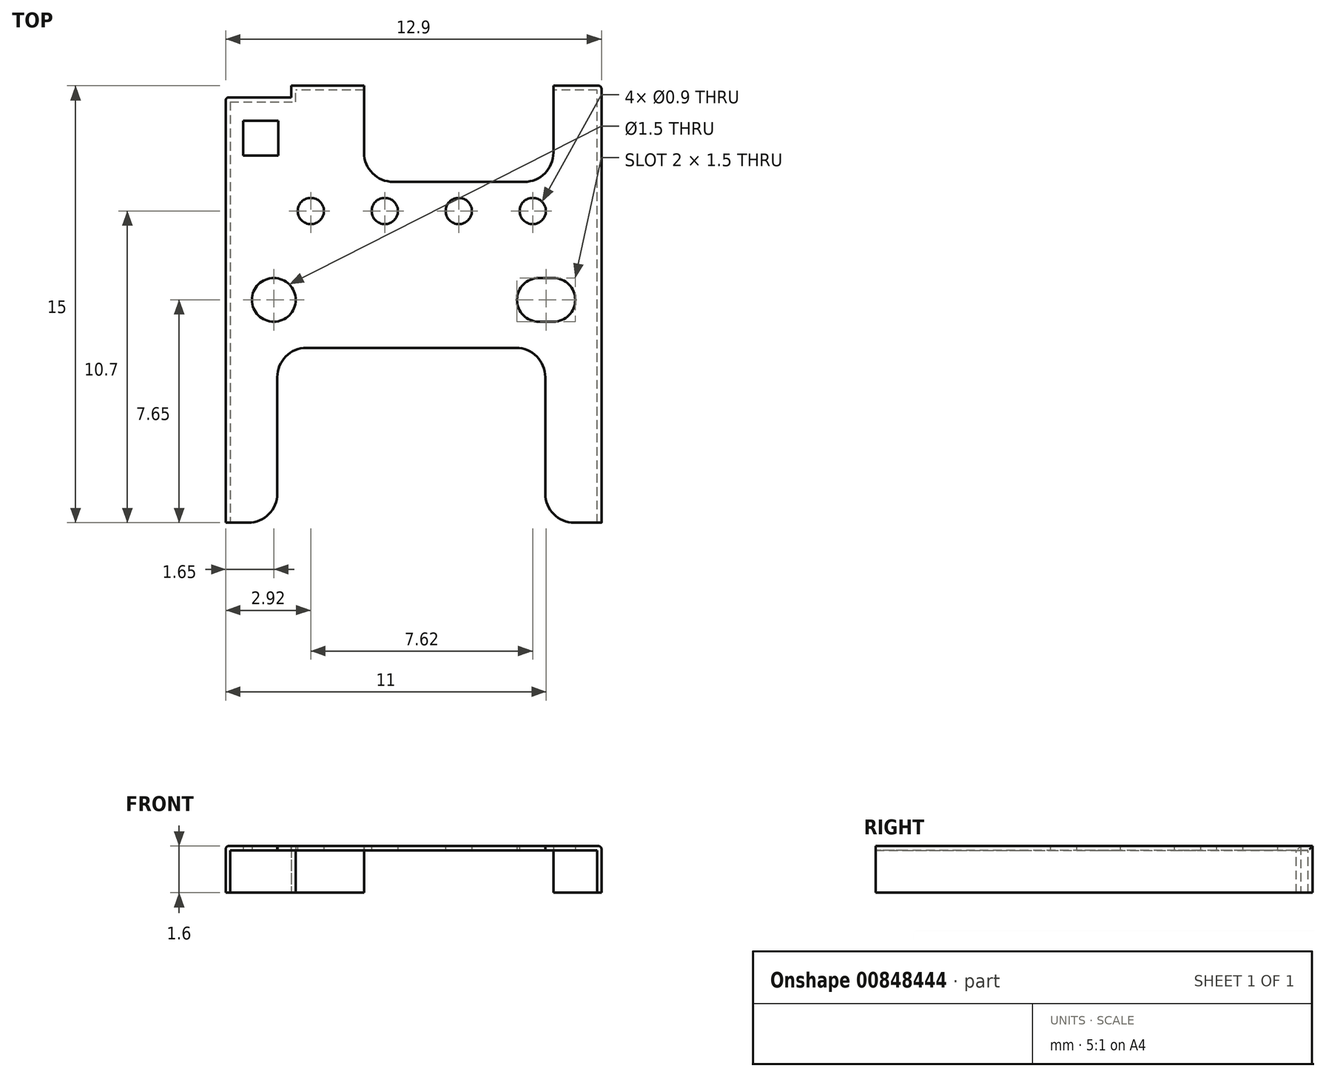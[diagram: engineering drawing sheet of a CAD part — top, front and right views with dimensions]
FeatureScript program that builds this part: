
annotation { "Feature Type Name" : "Feature", "Feature Type Description" : "" }
export const myFeature = defineFeature(function(context is Context, id is Id, definition is map)
    precondition{}
    {
        {
            var Q0;
            Q0=qCreatedBy(makeId("Top.planeOp"),FACE);
            var sketch = newSketch(context, id + "F0", { "sketchPlane" : qUnion([Q0])});
            skLineSegment(sketch, "E0.bottom", {"start": v(0, 0) * mm, "end": v(1.77, 0) * mm});
            skLineSegment(sketch, "E0.top", {"start": v(2.25, 15) * mm, "end": v(4.75, 15) * mm});
            skLineSegment(sketch, "E0.left", {"start": v(0, 0) * mm, "end": v(0, 14.6) * mm});
            skLineSegment(sketch, "E0.right", {"start": v(12.9, 0) * mm, "end": v(12.9, 15) * mm});
            skLineSegment(sketch, "E1.top", {"start": v(4.75, 11.7) * mm, "end": v(11.25, 11.7) * mm});
            skLineSegment(sketch, "E1.left", {"start": v(4.75, 15) * mm, "end": v(4.75, 11.7) * mm});
            skLineSegment(sketch, "E1.right", {"start": v(11.25, 15) * mm, "end": v(11.25, 11.7) * mm});
            skLineSegment(sketch, "E2.trimOffspring", {"start": v(11.25, 15) * mm, "end": v(12.9, 15) * mm});
            skLineSegment(sketch, "E3.bottom", {"start": v(0.6, 13.8) * mm, "end": v(1.8, 13.8) * mm});
            skLineSegment(sketch, "E3.top", {"start": v(0.6, 12.6) * mm, "end": v(1.8, 12.6) * mm});
            skLineSegment(sketch, "E3.left", {"start": v(0.6, 13.8) * mm, "end": v(0.6, 12.6) * mm});
            skLineSegment(sketch, "E3.right", {"start": v(1.8, 13.8) * mm, "end": v(1.8, 12.6) * mm});
            skLineSegment(sketch, "E4.top", {"start": v(0, 14.6) * mm, "end": v(2.25, 14.6) * mm});
            skLineSegment(sketch, "E4.right", {"start": v(2.25, 15) * mm, "end": v(2.25, 14.6) * mm});
            skCircle(sketch, "E5", {"center": v(5.46, 10.7) * mm, "radius": 0.45 * mm});
            skCircle(sketch, "E6", {"center": v(8, 10.7) * mm, "radius": 0.45 * mm});
            skCircle(sketch, "E7", {"center": v(10.54, 10.7) * mm, "radius": 0.45 * mm});
            skLineSegment(sketch, "E8", {"start": v(8, 11.7) * mm, "end": v(8, 10.7) * mm, "construction": true});
            skLineSegment(sketch, "E9", {"start": v(8, 10.7) * mm, "end": v(10.54, 10.7) * mm, "construction": true});
            skLineSegment(sketch, "E10", {"start": v(8, 10.7) * mm, "end": v(5.46, 10.7) * mm, "construction": true});
            skArc(sketch, "E11", {"start": v(11.25, 6.9) * mm, "mid": v(12, 7.65) * mm, "end": v(11.25, 8.4) * mm});
            skLineSegment(sketch, "E12", {"start": v(11.25, 7.65) * mm, "end": v(10.75, 7.65) * mm, "construction": true});
            skArc(sketch, "E13", {"start": v(10.75, 8.4) * mm, "mid": v(10, 7.65) * mm, "end": v(10.75, 6.9) * mm});
            skLineSegment(sketch, "E14", {"start": v(10.75, 8.4) * mm, "end": v(11.25, 8.4) * mm});
            skLineSegment(sketch, "E15", {"start": v(10.75, 6.9) * mm, "end": v(11.25, 6.9) * mm});
            skLineSegment(sketch, "E16", {"start": v(10.75, 7.65) * mm, "end": v(1.65, 7.65) * mm, "construction": true});
            skCircle(sketch, "E17", {"center": v(1.65, 7.65) * mm, "radius": 0.75 * mm});
            skLineSegment(sketch, "E18.top", {"start": v(1.77, 6) * mm, "end": v(10.97, 6) * mm});
            skLineSegment(sketch, "E18.left", {"start": v(1.77, 0) * mm, "end": v(1.77, 6) * mm});
            skLineSegment(sketch, "E18.right", {"start": v(10.97, 0) * mm, "end": v(10.97, 6) * mm});
            skCircle(sketch, "E19", {"center": v(2.92, 10.7) * mm, "radius": 0.45 * mm});
            skLineSegment(sketch, "E20", {"start": v(5.46, 10.7) * mm, "end": v(2.92, 10.7) * mm, "construction": true});
            skLineSegment(sketch, "E21.trimOffspring", {"start": v(10.97, 0) * mm, "end": v(12.9, 0) * mm});
            skSolve(sketch);
        }
        {
            var Q0;
            Q0=makeQuery(id+"F0.imprint","IMPRINT",FACE,{"disambiguationData":[TD([[makeQuery(id+"F0.imprint","IMPRINT",EDGE,{"derivedFrom":sQuery(id+"F0.wireOp",EDGE,"E0.bottom")}),1.0]])]});
            extrude(context, id + "F1", {"entities" : qUnion([Q0]), "depth" : 0.15 * mm, "offsetDistance" : 25 * mm});
        }
        {
            var Q0;
            Q0=makeQuery(id+"F1.opExtrude","CAP_FACE",FACE,{"disambiguationData":[OSD([sQuery(id+"F0.wireOp",EDGE,"E0.bottom"),sQuery(id+"F0.wireOp",EDGE,"E0.top"),sQuery(id+"F0.wireOp",EDGE,"E0.left"),sQuery(id+"F0.wireOp",EDGE,"E0.right"),sQuery(id+"F0.wireOp",EDGE,"E1.top"),sQuery(id+"F0.wireOp",EDGE,"E1.left"),sQuery(id+"F0.wireOp",EDGE,"E1.right"),sQuery(id+"F0.wireOp",EDGE,"E2.trimOffspring"),sQuery(id+"F0.wireOp",EDGE,"E3.bottom"),sQuery(id+"F0.wireOp",EDGE,"E3.top"),sQuery(id+"F0.wireOp",EDGE,"E3.left"),sQuery(id+"F0.wireOp",EDGE,"E3.right"),sQuery(id+"F0.wireOp",EDGE,"E4.top"),sQuery(id+"F0.wireOp",EDGE,"E4.right"),sQuery(id+"F0.wireOp",EDGE,"E5"),sQuery(id+"F0.wireOp",EDGE,"E6"),sQuery(id+"F0.wireOp",EDGE,"E7"),sQuery(id+"F0.wireOp",EDGE,"E11"),sQuery(id+"F0.wireOp",EDGE,"E13"),sQuery(id+"F0.wireOp",EDGE,"E14"),sQuery(id+"F0.wireOp",EDGE,"E15"),sQuery(id+"F0.wireOp",EDGE,"E17"),sQuery(id+"F0.wireOp",EDGE,"E18.top"),sQuery(id+"F0.wireOp",EDGE,"E18.left"),sQuery(id+"F0.wireOp",EDGE,"E18.right"),sQuery(id+"F0.wireOp",EDGE,"E19"),sQuery(id+"F0.wireOp",EDGE,"E21.trimOffspring")])],"isStart":true});
            var sketch = newSketch(context, id + "F2", { "sketchPlane" : qUnion([Q0])});
            skLineSegment(sketch, "E22.bottom", {"start": v(12.9, 0) * mm, "end": v(12.75, 0) * mm});
            skLineSegment(sketch, "E22.top", {"start": v(12.9, -15) * mm, "end": v(12.75, -15) * mm});
            skLineSegment(sketch, "E22.left", {"start": v(12.9, 0) * mm, "end": v(12.9, -15) * mm});
            skLineSegment(sketch, "E22.right", {"start": v(12.75, 0) * mm, "end": v(12.75, -15) * mm});
            skLineSegment(sketch, "E23.bottom", {"start": v(12.75, -14.85) * mm, "end": v(11.25, -14.85) * mm});
            skLineSegment(sketch, "E23.top", {"start": v(12.75, -15) * mm, "end": v(11.25, -15) * mm});
            skLineSegment(sketch, "E23.left", {"start": v(12.75, -14.85) * mm, "end": v(12.75, -15) * mm});
            skLineSegment(sketch, "E23.right", {"start": v(11.25, -14.85) * mm, "end": v(11.25, -15) * mm});
            skLineSegment(sketch, "E24.bottom", {"start": v(4.75, -14.85) * mm, "end": v(2.25, -14.85) * mm});
            skLineSegment(sketch, "E24.top", {"start": v(4.75, -15) * mm, "end": v(2.25, -15) * mm});
            skLineSegment(sketch, "E24.left", {"start": v(4.75, -14.85) * mm, "end": v(4.75, -15) * mm});
            skLineSegment(sketch, "E24.right", {"start": v(2.25, -14.85) * mm, "end": v(2.25, -15) * mm});
            skLineSegment(sketch, "E25.bottom", {"start": v(0, -14.6) * mm, "end": v(2.25, -14.6) * mm});
            skLineSegment(sketch, "E25.top", {"start": v(0, -14.45) * mm, "end": v(2.25, -14.45) * mm});
            skLineSegment(sketch, "E25.left", {"start": v(0, -14.6) * mm, "end": v(0, -14.45) * mm});
            skLineSegment(sketch, "E25.right", {"start": v(2.25, -14.6) * mm, "end": v(2.25, -14.45) * mm});
            skLineSegment(sketch, "E26.bottom", {"start": v(2.25, -14.45) * mm, "end": v(2.4, -14.45) * mm});
            skLineSegment(sketch, "E26.top", {"start": v(2.25, -14.85) * mm, "end": v(2.4, -14.85) * mm});
            skLineSegment(sketch, "E26.left", {"start": v(2.25, -14.45) * mm, "end": v(2.25, -14.85) * mm});
            skLineSegment(sketch, "E26.right", {"start": v(2.4, -14.45) * mm, "end": v(2.4, -14.85) * mm});
            skLineSegment(sketch, "E27.bottom", {"start": v(0.15, -14.45) * mm, "end": v(0, -14.45) * mm});
            skLineSegment(sketch, "E27.top", {"start": v(0.15, 0) * mm, "end": v(0, 0) * mm});
            skLineSegment(sketch, "E27.left", {"start": v(0.15, -14.45) * mm, "end": v(0.15, 0) * mm});
            skLineSegment(sketch, "E27.right", {"start": v(0, -14.45) * mm, "end": v(0, 0) * mm});
            skSolve(sketch);
        }
        {
            var Q0;
            {var subQ1=sQuery(id+"F2.wireOp",EDGE,"E22.bottom");Q0=makeQuery(id+"F2.imprint","IMPRINT",FACE,{"disambiguationData":[TD([[makeQuery(id+"F2.imprint","IMPRINT",EDGE,{"derivedFrom":subQ1}),-1.0]])]});}
            var Q1;
            {var subQ2=sQuery(id+"F2.wireOp",EDGE,"E23.bottom");Q1=makeQuery(id+"F2.imprint","IMPRINT",FACE,{"disambiguationData":[TD([[makeQuery(id+"F2.imprint","IMPRINT",EDGE,{"derivedFrom":subQ2}),1.0]])]});}
            var Q2;
            Q2=makeQuery(id+"F2.imprint","IMPRINT",FACE,{"disambiguationData":[TD([[makeQuery(id+"F2.imprint","IMPRINT",EDGE,{"derivedFrom":sQuery(id+"F2.wireOp",EDGE,"E24.top")}),1.0]])]});
            var Q3;
            Q3=makeQuery(id+"F2.imprint","IMPRINT",FACE,{"disambiguationData":[TD([[makeQuery(id+"F2.imprint","IMPRINT",EDGE,{"derivedFrom":sQuery(id+"F2.wireOp",EDGE,"E25.right")}),-1.0]])]});
            var Q4;
            Q4=makeQuery(id+"F2.imprint","IMPRINT",FACE,{"disambiguationData":[TD([[makeQuery(id+"F2.imprint","IMPRINT",EDGE,{"derivedFrom":sQuery(id+"F2.wireOp",EDGE,"E25.bottom")}),1.0]])]});
            var Q5;
            Q5=makeQuery(id+"F2.imprint","IMPRINT",FACE,{"disambiguationData":[TD([[makeQuery(id+"F2.imprint","IMPRINT",EDGE,{"derivedFrom":sQuery(id+"F2.wireOp",EDGE,"E27.top")}),-1.0]])]});
            extrude(context, id + "F3", {"entities" : qUnion([Q0, Q1, Q2, Q3, Q4, Q5]), "operationType" : NewBodyOperationType.ADD, "depth" : 1.45 * mm, "offsetDistance" : 25 * mm});
        }
        {
            var Q0;
            Q0=makeQuery(id+"F1.opExtrude","SWEPT_EDGE",EDGE,{"disambiguationData":[OSD([sQuery(id+"F0.wireOp",EDGE,"E18.top"),sQuery(id+"F0.wireOp",EDGE,"E18.left")])]});
            var Q1;
            Q1=makeQuery(id+"F1.opExtrude","SWEPT_EDGE",EDGE,{"disambiguationData":[OSD([sQuery(id+"F0.wireOp",EDGE,"E0.bottom"),sQuery(id+"F0.wireOp",EDGE,"E18.left")])]});
            var Q2;
            Q2=makeQuery(id+"F1.opExtrude","SWEPT_EDGE",EDGE,{"disambiguationData":[OSD([sQuery(id+"F0.wireOp",EDGE,"E18.top"),sQuery(id+"F0.wireOp",EDGE,"E18.right")])]});
            var Q3;
            Q3=makeQuery(id+"F1.opExtrude","SWEPT_EDGE",EDGE,{"disambiguationData":[OSD([sQuery(id+"F0.wireOp",EDGE,"E18.right"),sQuery(id+"F0.wireOp",EDGE,"E21.trimOffspring")])]});
            var Q4;
            Q4=makeQuery(id+"F1.opExtrude","SWEPT_EDGE",EDGE,{"disambiguationData":[OSD([sQuery(id+"F0.wireOp",EDGE,"E1.top"),sQuery(id+"F0.wireOp",EDGE,"E1.left")])]});
            var Q5;
            Q5=makeQuery(id+"F1.opExtrude","SWEPT_EDGE",EDGE,{"disambiguationData":[OSD([sQuery(id+"F0.wireOp",EDGE,"E1.top"),sQuery(id+"F0.wireOp",EDGE,"E1.right")])]});
            fillet(context, id + "F4", {"entities" : qUnion([Q0, Q1, Q2, Q3, Q4, Q5]), "radius" : 1 * mm, "tangentPropagation" : true, "allowEdgeOverflow" : false});
        }
        {
            var Q0;
            Q0=makeQuery(id+"F1.opExtrude","CAP_EDGE",EDGE,{"disambiguationData":[OSD([sQuery(id+"F0.wireOp",EDGE,"E0.right")])],"isStart":false});
            var Q1;
            Q1=makeQuery(id+"F1.opExtrude","CAP_EDGE",EDGE,{"disambiguationData":[OSD([sQuery(id+"F0.wireOp",EDGE,"E0.left")])],"isStart":false});
            var Q2;
            Q2=makeQuery(id+"F1.opExtrude","CAP_EDGE",EDGE,{"disambiguationData":[OSD([sQuery(id+"F0.wireOp",EDGE,"E0.top")])],"isStart":false});
            var Q3;
            Q3=makeQuery(id+"F3.boolean.opBoolean","MERGE",EDGE,{"derivedFrom":[makeQuery(id+"F1.opExtrude","SWEPT_EDGE",EDGE,{"disambiguationData":[OSD([sQuery(id+"F0.wireOp",EDGE,"E0.left"),sQuery(id+"F0.wireOp",EDGE,"E4.top")])]}),makeQuery(id+"F3.opExtrude","SWEPT_EDGE",EDGE,{"disambiguationData":[OSD([sQuery(id+"F2.wireOp",EDGE,"E25.bottom"),sQuery(id+"F2.wireOp",EDGE,"E25.left")])]})]});
            var Q4;
            Q4=makeQuery(id+"F3.boolean.opBoolean","MERGE",EDGE,{"derivedFrom":[makeQuery(id+"F1.opExtrude","SWEPT_EDGE",EDGE,{"disambiguationData":[OSD([sQuery(id+"F0.wireOp",EDGE,"E0.right"),sQuery(id+"F0.wireOp",EDGE,"E2.trimOffspring")])]}),makeQuery(id+"F3.opExtrude","SWEPT_EDGE",EDGE,{"disambiguationData":[OSD([sQuery(id+"F2.wireOp",EDGE,"E22.top"),sQuery(id+"F2.wireOp",EDGE,"E22.left")])]})]});
            fillet(context, id + "F5", {"entities" : qUnion([Q0, Q1, Q2, Q3, Q4]), "radius" : 0.1 * mm, "tangentPropagation" : true, "allowEdgeOverflow" : false});
        }
    });
